# Revit family: HTHB-OVLSER
name_source: partatom
category: Plumbing Fixtures
units: mm (PartAtom-declared; Revit-internal decimal feet)

## family parameters
Always vertical = Yes
Cut with Voids When Loaded = No
OmniClass Number = 23.45.00.00
OmniClass Title = Sanitary, Laundry, and Cleaning Equipment
Part Type = Normal
Room Calculation Point = No
Round Connector Dimension = Use Radius
Shared = No
Work Plane-Based = No

## types (2) — shared parameters
Activation = Sensor and push buttons
Apparent Load Phase 1 = 0 VA
Basin Material = Metal - Steel - Stainless - Chrome
Body Material = Metal - Steel - Stainless - Chrome
Bottle Apparent Load Phase 1 = 0 VA
Bottle Voltage = 0 V
Bottle Water Service Flow = 0 GPM
Bottle Water Service Flow Out = 0 GPM
Bottle Water Service Size Radius = 0' - 0 5/8"
Bubbler = Double bubbler
Bubbler Material = Metal - Steel - Stainless - Chrome
CW Connection = Yes
Chiller = HTHB-OVLSER-I
Chiller Option = Yes
Cooler Depth = 1' - 6"
Cooler Width = 5' - 0 1/8"
Description = Water Cooler
HW Connection = No
Lower Unit Rim Height = 2' - 10"
Manufacturer = Halsey Taylor
Model = OVL-II HTHB-OVLSER-I
Mounting = MFWS230
Panel Material = Metal - Steel - Stainless - Chrome
Plastic One Material = Metal - Steel - Stainless - Color 3
Plastic Two Material = Metal - Steel - Stainless - Aztec Gold
Sanitary Connector Description = Sanitary Connection
Sanitary Service Size Radius = 0' - 0 5/8"
Type = Bi-level with bottle filler
URL = http://www.halseytaylor.com
Upper Unit Rim Height = 3' - 4"
Vent Connection = No
Version = 1.0.0.0
Voltage = 0 V
Volts/Hertz = 115V/60Hz
Wall Plate Material = Metal - Steel - Stainless - Chrome
Waste Connection = Yes
Water Connector Description = Water Supply
Water Out Connection Description = Water Return
Water Service Flow = 0 GPM
Water Service Flow Out = 0 GPM
Water Service Size Radius = 0' - 0 1/4"

## per-type parameters (varying)
| type | Filter |
| HTHB-OVLSER | NONE |
| HTHBWF-OVLSER-I | YES |

## geometry (parser evidence)
native form markers: Sweep x3
no freeform markers — native parametric forms only
